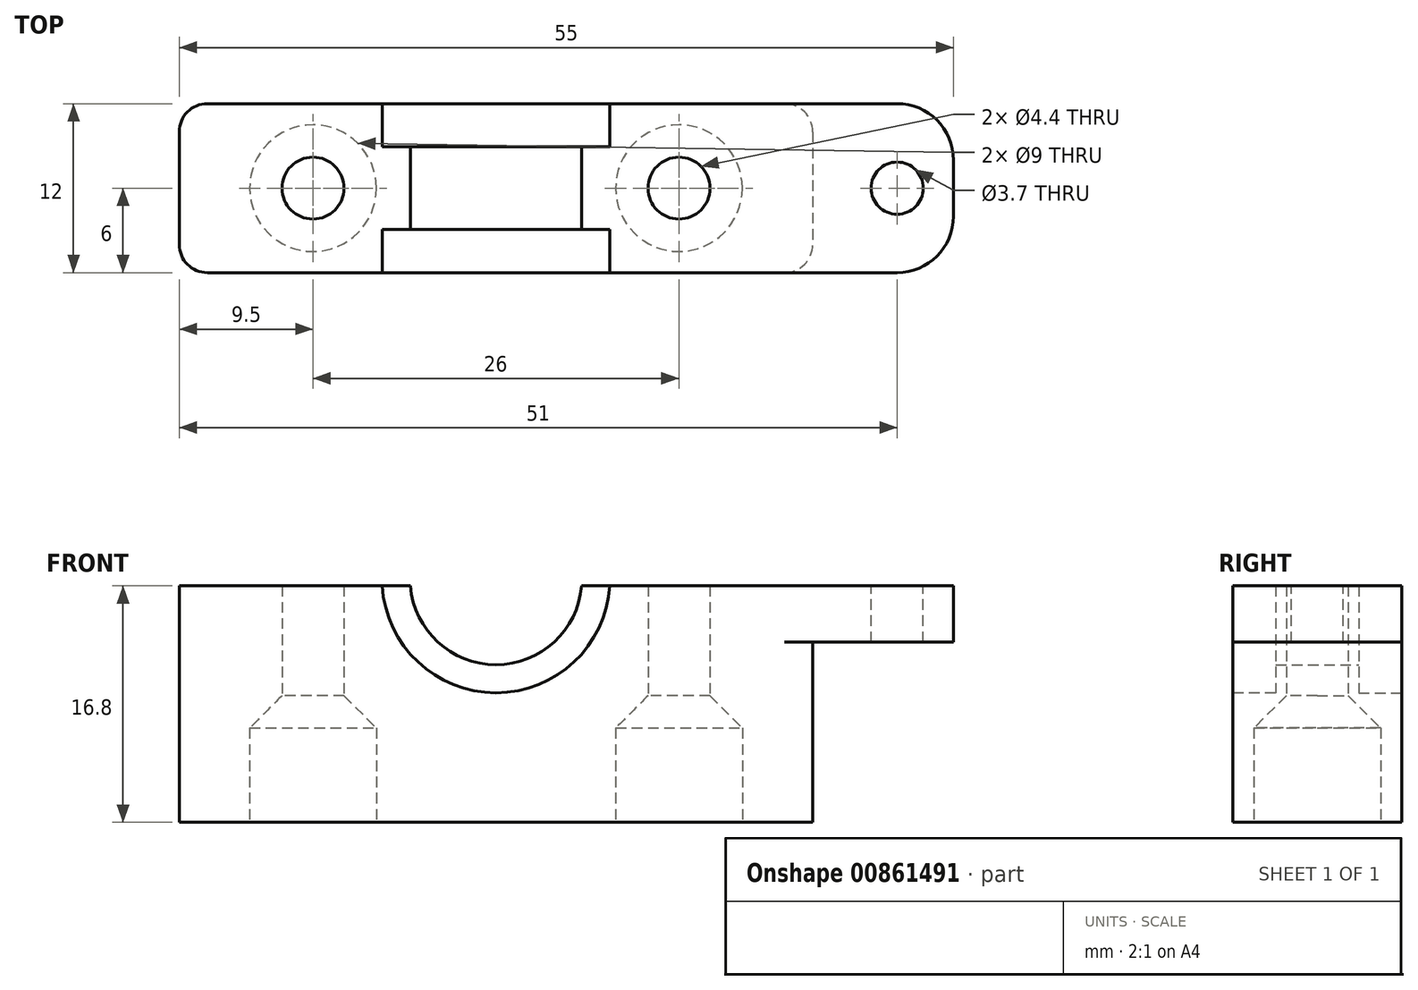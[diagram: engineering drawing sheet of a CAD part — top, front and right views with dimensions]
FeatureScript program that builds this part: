
annotation { "Feature Type Name" : "Feature", "Feature Type Description" : "" }
export const myFeature = defineFeature(function(context is Context, id is Id, definition is map)
    precondition{}
    {
        {
            var Q0;
            Q0=qCreatedBy(makeId("Top.planeOp"),FACE);
            var sketch = newSketch(context, id + "F0", { "sketchPlane" : qUnion([Q0])});
            skLineSegment(sketch, "E0.bottom", {"start": v(-22.5, 6) * mm, "end": v(22.5, 6) * mm});
            skLineSegment(sketch, "E0.top", {"start": v(-22.5, -6) * mm, "end": v(22.5, -6) * mm});
            skLineSegment(sketch, "E0.left", {"start": v(-22.5, 6) * mm, "end": v(-22.5, -6) * mm});
            skLineSegment(sketch, "E0.right", {"start": v(22.5, 6) * mm, "end": v(22.5, -6) * mm});
            skCircle(sketch, "E1", {"center": v(-13, 0) * mm, "radius": 2.2 * mm});
            skCircle(sketch, "E2", {"center": v(13, 0) * mm, "radius": 2.2 * mm});
            skSolve(sketch);
        }
        {
            var Q0;
            Q0=qSketchRegion(id+"F0",true);
            extrude(context, id + "F1", {"entities" : qUnion([Q0]), "depth" : 16.8 * mm, "offsetDistance" : 25 * mm});
        }
        {
            var Q0;
            Q0=makeQuery(id+"F1.opExtrude","SWEPT_FACE",FACE,{"disambiguationData":[OSD([sQuery(id+"F0.wireOp",EDGE,"E0.bottom")])]});
            var sketch = newSketch(context, id + "F2", { "sketchPlane" : qUnion([Q0])});
            skPoint(sketch, "E3.0", {"position": v(0, 16.8) * mm});
            skLineSegment(sketch, "E4.0", {"start": v(22.5, 16.8) * mm, "end": v(-22.5, 16.8) * mm});
            skCircle(sketch, "E5", {"center": v(0, 17.3) * mm, "radius": 6.1 * mm});
            skSolve(sketch);
        }
        {
            var Q0;
            Q0=qSketchRegion(id+"F2",true);
            extrude(context, id + "F3", {"entities" : qUnion([Q0]), "operationType" : NewBodyOperationType.REMOVE, "endBound" : BoundingType.THROUGH_ALL, "oppositeDirection" : true, "depth" : 25 * mm, "offsetDistance" : 25 * mm});
        }
        {
            var Q0;
            Q0=makeQuery(id+"F1.opExtrude","SWEPT_FACE",FACE,{"disambiguationData":[OSD([sQuery(id+"F0.wireOp",EDGE,"E0.bottom")])]});
            var sketch = newSketch(context, id + "F4", { "sketchPlane" : qUnion([Q0])});
            skArc(sketch, "E6.0", {"start": v(-6.08, 16.8) * mm, "mid": v(0, 11.2) * mm, "end": v(6.08, 16.8) * mm});
            skCircle(sketch, "E7", {"center": v(0, 17.3) * mm, "radius": 8.1 * mm});
            skSolve(sketch);
        }
        {
            var Q0;
            Q0=qSketchRegion(id+"F4",true);
            extrude(context, id + "F5", {"entities" : qUnion([Q0]), "operationType" : NewBodyOperationType.REMOVE, "oppositeDirection" : true, "depth" : 3.05 * mm, "offsetDistance" : 25 * mm});
        }
        {
            var Q0;
            Q0=makeQuery(id+"F1.opExtrude","SWEPT_FACE",FACE,{"disambiguationData":[OSD([sQuery(id+"F0.wireOp",EDGE,"E0.top")])]});
            var sketch = newSketch(context, id + "F6", { "sketchPlane" : qUnion([Q0])});
            skArc(sketch, "E8.0", {"start": v(6.08, 16.8) * mm, "mid": v(0, 11.2) * mm, "end": v(-6.08, 16.8) * mm});
            skCircle(sketch, "E9", {"center": v(0, 17.3) * mm, "radius": 8.1 * mm});
            skSolve(sketch);
        }
        {
            var Q0;
            Q0=qSketchRegion(id+"F6",true);
            extrude(context, id + "F7", {"entities" : qUnion([Q0]), "operationType" : NewBodyOperationType.REMOVE, "oppositeDirection" : true, "depth" : 3.05 * mm, "offsetDistance" : 25 * mm});
        }
        {
            var Q0;
            Q0=makeQuery(id+"FNERBGZvCK0uBXY_1.boolean.opBoolean","MERGE",FACE,{"derivedFrom":[makeQuery(id+"F1.opExtrude","CAP_FACE",FACE,{"disambiguationData":[OSD([sQuery(id+"F0.wireOp",EDGE,"E0.bottom"),sQuery(id+"F0.wireOp",EDGE,"E0.top"),sQuery(id+"F0.wireOp",EDGE,"E0.left"),sQuery(id+"F0.wireOp",EDGE,"E0.right"),sQuery(id+"F0.wireOp",EDGE,"E1"),sQuery(id+"F0.wireOp",EDGE,"E2")])],"isStart":true}),makeQuery(id+"FNERBGZvCK0uBXY_1.opExtrude","CAP_FACE",FACE,{"disambiguationData":[OSD([sQuery(id+"FdTTqbgPQmqQFHr_1.wireOp",EDGE,"NFuGmGHk-Y8jQ-TEMF-p6EN-6jji0c57RYxW"),sQuery(id+"FdTTqbgPQmqQFHr_1.wireOp",EDGE,"flPMFt8A-b7tU-MbQ5-79Tx-EWiZWgdHCNE5"),sQuery(id+"FdTTqbgPQmqQFHr_1.wireOp",EDGE,"i2FXRTVV-8gz3-Wmie-WVd2-92qPCMGCYP3O"),sQuery(id+"FdTTqbgPQmqQFHr_1.wireOp",EDGE,"47zcAhAI-3MiS-mLvU-s0xS-0LrZlLgu21tJ"),sQuery(id+"FdTTqbgPQmqQFHr_1.wireOp",EDGE,"KhqW6fxU-w8Nb-SH3q-u9D0-n6Mz10YSgWkf"),sQuery(id+"FdTTqbgPQmqQFHr_1.wireOp",EDGE,"kxzdFVXP-5BfB-93dJ-oiJD-XY34wRmJZHPV")])],"isStart":true})]});
            var sketch = newSketch(context, id + "F8", { "sketchPlane" : qUnion([Q0])});
            skCircle(sketch, "E10.0", {"center": v(-13, 0) * mm, "radius": 2.2 * mm});
            skCircle(sketch, "E11.0", {"center": v(13, 0) * mm, "radius": 2.2 * mm});
            skCircle(sketch, "E12", {"center": v(-13, 0) * mm, "radius": 4.5 * mm});
            skCircle(sketch, "E13", {"center": v(13, 0) * mm, "radius": 4.5 * mm});
            skSolve(sketch);
        }
        {
            var Q0;
            Q0=qSketchRegion(id+"F8",true);
            extrude(context, id + "F9", {"entities" : qUnion([Q0]), "operationType" : NewBodyOperationType.REMOVE, "oppositeDirection" : true, "depth" : 9 * mm, "offsetDistance" : 25 * mm});
        }
        {
            var Q0;
            Q0=makeQuery(id+"F9.boolean.opBoolean","COPY",EDGE,{"derivedFrom":makeQuery(id+"F9.opExtrude","CAP_EDGE",EDGE,{"disambiguationData":[OSD([sQuery(id+"F8.wireOp",EDGE,"E12")])],"isStart":false})});
            var Q1;
            Q1=makeQuery(id+"F9.boolean.opBoolean","COPY",EDGE,{"derivedFrom":makeQuery(id+"F9.opExtrude","CAP_EDGE",EDGE,{"disambiguationData":[OSD([sQuery(id+"F8.wireOp",EDGE,"E13")])],"isStart":false})});
            chamfer(context, id + "F10", {"entities" : qUnion([Q0, Q1]), "width" : 2.3 * mm, "tangentPropagation" : true});
        }
        {
            var Q0;
            Q0=makeQuery(id+"F1.opExtrude","SWEPT_EDGE",EDGE,{"disambiguationData":[OSD([sQuery(id+"F0.wireOp",EDGE,"E0.top"),sQuery(id+"F0.wireOp",EDGE,"E0.right")])]});
            var Q1;
            Q1=makeQuery(id+"F1.opExtrude","SWEPT_EDGE",EDGE,{"disambiguationData":[OSD([sQuery(id+"F0.wireOp",EDGE,"E0.top"),sQuery(id+"F0.wireOp",EDGE,"E0.left")])]});
            var Q2;
            Q2=makeQuery(id+"F1.opExtrude","SWEPT_EDGE",EDGE,{"disambiguationData":[OSD([sQuery(id+"F0.wireOp",EDGE,"E0.bottom"),sQuery(id+"F0.wireOp",EDGE,"E0.right")])]});
            var Q3;
            Q3=makeQuery(id+"F1.opExtrude","SWEPT_EDGE",EDGE,{"disambiguationData":[OSD([sQuery(id+"F0.wireOp",EDGE,"E0.bottom"),sQuery(id+"F0.wireOp",EDGE,"E0.left")])]});
            fillet(context, id + "F11", {"entities" : qUnion([Q0, Q1, Q2, Q3]), "radius" : 2 * mm, "tangentPropagation" : true, "allowEdgeOverflow" : false});
        }
        {
            var Q0;
            {var subQ0=sQuery(id+"F0.wireOp",EDGE,"E2");var subQ1=sQuery(id+"F0.wireOp",EDGE,"E0.top");var subQ2=sQuery(id+"F0.wireOp",EDGE,"E0.right");var subQ3=sQuery(id+"F0.wireOp",EDGE,"E0.bottom");Q0=makeQuery(id+"F3.boolean.opBoolean","SPLIT",FACE,{"disambiguationData":[TD([makeQuery(id+"F1.opExtrude","SWEPT_FACE",FACE,{"disambiguationData":[OSD([subQ2])]})])],"derivedFrom":makeQuery(id+"F1.opExtrude","CAP_FACE",FACE,{"disambiguationData":[OSD([subQ3,subQ1,sQuery(id+"F0.wireOp",EDGE,"E0.left"),subQ2,sQuery(id+"F0.wireOp",EDGE,"E1"),subQ0])],"isStart":false})});}
            var sketch = newSketch(context, id + "F12", { "sketchPlane" : qUnion([Q0])});
            skLineSegment(sketch, "E14.bottom", {"start": v(20.5, -6) * mm, "end": v(32.5, -6) * mm});
            skLineSegment(sketch, "E14.top", {"start": v(20.5, 6) * mm, "end": v(32.5, 6) * mm});
            skLineSegment(sketch, "E14.left", {"start": v(20.5, -6) * mm, "end": v(20.5, 6) * mm});
            skLineSegment(sketch, "E14.right", {"start": v(32.5, -6) * mm, "end": v(32.5, 6) * mm});
            skCircle(sketch, "E15", {"center": v(28.5, 0) * mm, "radius": 1.85 * mm});
            skPoint(sketch, "E15.centerSnap0", {"position": v(26.5, 6) * mm});
            skSolve(sketch);
        }
        {
            var Q0;
            Q0 = qSketchRegion(id + "F12", true);
            extrude(context, id + "F13", {"entities" : qUnion([Q0]), "operationType" : NewBodyOperationType.ADD, "oppositeDirection" : true, "depth" : 4 * mm, "offsetDistance" : 25 * mm});
        }
        {
            var Q0;
            Q0=makeQuery(id+"F13.opExtrude","SWEPT_EDGE",EDGE,{"disambiguationData":[OSD([sQuery(id+"F12.wireOp",EDGE,"E14.bottom"),sQuery(id+"F12.wireOp",EDGE,"E14.right")])]});
            var Q1;
            Q1=makeQuery(id+"F13.opExtrude","SWEPT_EDGE",EDGE,{"disambiguationData":[OSD([sQuery(id+"F12.wireOp",EDGE,"E14.top"),sQuery(id+"F12.wireOp",EDGE,"E14.right")])]});
            fillet(context, id + "F14", {"entities" : qUnion([Q0, Q1]), "radius" : 4 * mm, "tangentPropagation" : true, "allowEdgeOverflow" : false});
        }
    });
